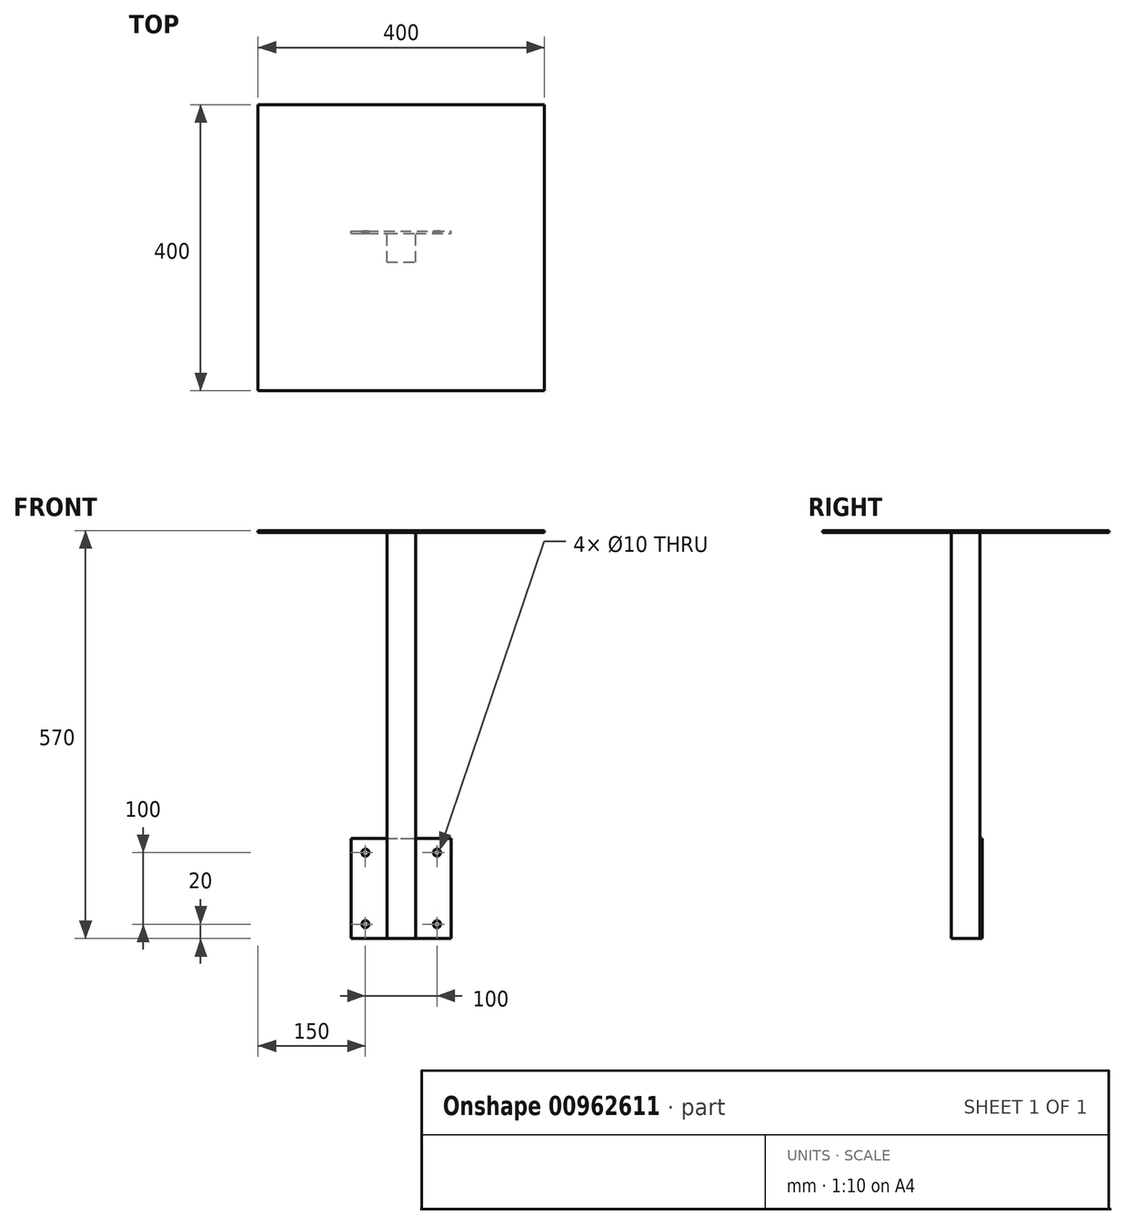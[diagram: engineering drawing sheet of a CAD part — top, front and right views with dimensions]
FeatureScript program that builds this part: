
annotation { "Feature Type Name" : "Feature", "Feature Type Description" : "" }
export const myFeature = defineFeature(function(context is Context, id is Id, definition is map)
    precondition{}
    {
        {
            var Q0;
            Q0=qCreatedBy(makeId("Front.planeOp"),FACE);
            cPlane(context, id + "F0", {"entities" : qUnion([Q0]), "cplaneType" : CPlaneType.OFFSET, "offset" : 46 * mm, "width" : 150 * mm, "height" : 150 * mm});
        }
        {
            var Q0;
            Q0=qCreatedBy(id+"F0.planeOp",FACE);
            var sketch = newSketch(context, id + "F1", { "sketchPlane" : qUnion([Q0])});
            skLineSegment(sketch, "E0", {"start": v(0, 1000) * mm, "end": v(0, 0) * mm, "construction": true});
            skLineSegment(sketch, "E1.bottom", {"start": v(-70, 1070) * mm, "end": v(70, 1070) * mm});
            skLineSegment(sketch, "E1.left", {"start": v(-70, 1070) * mm, "end": v(-70, 930) * mm});
            skLineSegment(sketch, "E1.right", {"start": v(70, 1070) * mm, "end": v(70, 930) * mm});
            skLineSegment(sketch, "E2", {"start": v(0, 1070) * mm, "end": v(0, 930) * mm, "construction": true});
            skLineSegment(sketch, "E3", {"start": v(-70, 930) * mm, "end": v(70, 930) * mm});
            skLineSegment(sketch, "E4.bottom", {"start": v(50, 950) * mm, "end": v(-50, 950) * mm, "construction": true});
            skLineSegment(sketch, "E4.top", {"start": v(50, 1050) * mm, "end": v(-50, 1050) * mm, "construction": true});
            skLineSegment(sketch, "E4.left", {"start": v(50, 950) * mm, "end": v(50, 1050) * mm, "construction": true});
            skLineSegment(sketch, "E4.right", {"start": v(-50, 950) * mm, "end": v(-50, 1050) * mm, "construction": true});
            skPoint(sketch, "E4.middle", {"position": v(0, 1000) * mm});
            skCircle(sketch, "E5", {"center": v(-50, 1050) * mm, "radius": 5 * mm});
            skCircle(sketch, "E6", {"center": v(50, 1050) * mm, "radius": 5 * mm});
            skCircle(sketch, "E7", {"center": v(-50, 950) * mm, "radius": 5 * mm});
            skCircle(sketch, "E8", {"center": v(50, 950) * mm, "radius": 5 * mm});
            skSolve(sketch);
        }
        {
            var Q0;
            Q0 = qSketchRegion(id + "F1", true);
            extrude(context, id + "F2", {"entities" : qUnion([Q0]), "depth" : 3 * mm, "offsetDistance" : 25 * mm});
        }
        {
            var Q0;
            Q0=makeQuery(id+"F2.opExtrude","CAP_FACE",FACE,{"disambiguationData":[OSD([sQuery(id+"F1.wireOp",EDGE,"E1.bottom"),sQuery(id+"F1.wireOp",EDGE,"E1.left"),sQuery(id+"F1.wireOp",EDGE,"E1.right"),sQuery(id+"F1.wireOp",EDGE,"E3")])],"isStart":false});
            var sketch = newSketch(context, id + "F3", { "sketchPlane" : qUnion([Q0])});
            skLineSegment(sketch, "E9", {"start": v(-70, 1000) * mm, "end": v(70, 1000) * mm, "construction": true});
            skLineSegment(sketch, "E10", {"start": v(0, 930) * mm, "end": v(0, 1497) * mm, "construction": true});
            skLineSegment(sketch, "E11", {"start": v(-20, 1497) * mm, "end": v(-20, 930) * mm});
            skLineSegment(sketch, "E12", {"start": v(-20, 930) * mm, "end": v(20, 930) * mm});
            skLineSegment(sketch, "E13", {"start": v(20, 930) * mm, "end": v(20, 1497) * mm});
            skLineSegment(sketch, "E14", {"start": v(-20, 1497) * mm, "end": v(20, 1497) * mm});
            skSolve(sketch);
        }
        {
            var Q0;
            Q0 = qSketchRegion(id + "F3", true);
            extrude(context, id + "F4", {"entities" : qUnion([Q0]), "operationType" : NewBodyOperationType.ADD, "depth" : 40 * mm, "offsetDistance" : 25 * mm});
        }
        {
            var Q0;
            Q0=makeQuery(id+"F4.opExtrude","SWEPT_FACE",FACE,{"disambiguationData":[OSD([sQuery(id+"F3.wireOp",EDGE,"E14")])]});
            var sketch = newSketch(context, id + "F5", { "sketchPlane" : qUnion([Q0])});
            skLineSegment(sketch, "E15", {"start": v(-20, -69) * mm, "end": v(139.36, -69) * mm, "construction": true});
            skLineSegment(sketch, "E16", {"start": v(0, -49) * mm, "end": v(0, -172.32) * mm, "construction": true});
            skLineSegment(sketch, "E17.bottom", {"start": v(200, -269) * mm, "end": v(-200, -269) * mm});
            skLineSegment(sketch, "E17.top", {"start": v(200, 131) * mm, "end": v(-200, 131) * mm});
            skLineSegment(sketch, "E17.left", {"start": v(200, -269) * mm, "end": v(200, 131) * mm});
            skLineSegment(sketch, "E17.right", {"start": v(-200, -269) * mm, "end": v(-200, 131) * mm});
            skPoint(sketch, "E17.middle", {"position": v(0, -69) * mm});
            skSolve(sketch);
        }
        {
            var Q0;
            Q0 = qSketchRegion(id + "F5", true);
            extrude(context, id + "F6", {"entities" : qUnion([Q0]), "depth" : 3 * mm, "offsetDistance" : 25 * mm});
        }
    });
